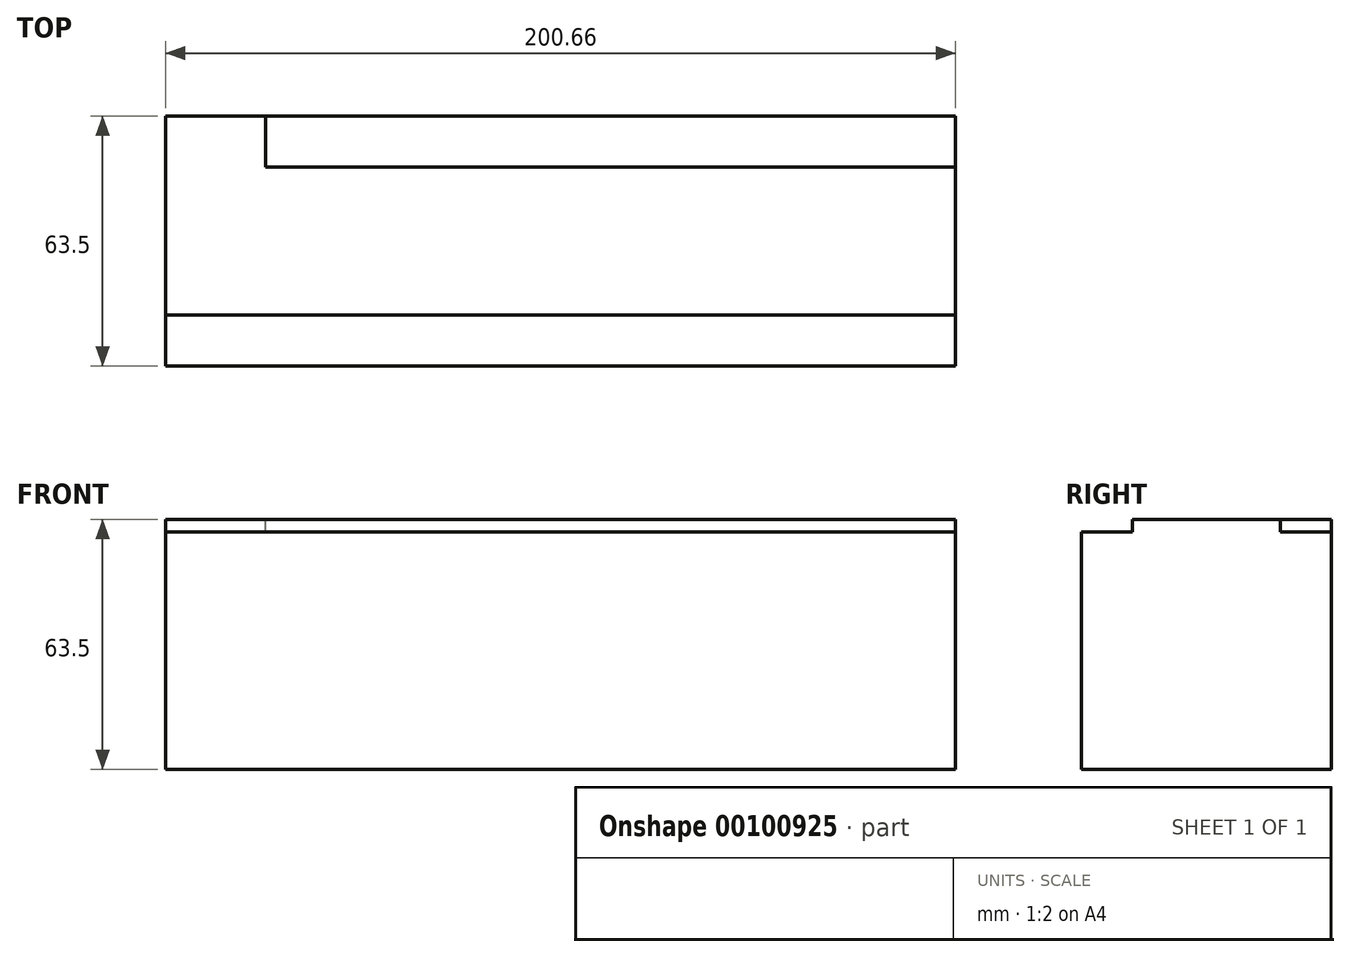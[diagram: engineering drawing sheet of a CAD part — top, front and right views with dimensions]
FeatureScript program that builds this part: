
annotation { "Feature Type Name" : "Feature", "Feature Type Description" : "" }
export const myFeature = defineFeature(function(context is Context, id is Id, definition is map)
    precondition{}
    {
        {
            var Q0;
            Q0=qCreatedBy(makeId("Top.planeOp"),FACE);
            var sketch = newSketch(context, id + "F0", { "sketchPlane" : qUnion([Q0])});
            skLineSegment(sketch, "E0.bottom", {"start": v(0, 0) * mm, "end": v(-200.66, 0) * mm});
            skLineSegment(sketch, "E0.top", {"start": v(0, 63.5) * mm, "end": v(-200.66, 63.5) * mm});
            skLineSegment(sketch, "E0.left", {"start": v(0, 0) * mm, "end": v(0, 63.5) * mm});
            skLineSegment(sketch, "E0.right", {"start": v(-200.66, 0) * mm, "end": v(-200.66, 63.5) * mm});
            skSolve(sketch);
        }
        {
            var Q0;
            Q0 = qSketchRegion(id + "F0", true);
            extrude(context, id + "F1", {"entities" : qUnion([Q0]), "oppositeDirection" : true, "depth" : 63.5 * mm});
        }
        {
            var Q0;
            Q0=makeQuery(id+"F1.opExtrude","CAP_FACE",FACE,{"disambiguationData":[OSD([sQuery(id+"F0.wireOp",EDGE,"E0.bottom"),sQuery(id+"F0.wireOp",EDGE,"E0.top"),sQuery(id+"F0.wireOp",EDGE,"E0.left"),sQuery(id+"F0.wireOp",EDGE,"E0.right")])],"isStart":true});
            var sketch = newSketch(context, id + "F2", { "sketchPlane" : qUnion([Q0])});
            skLineSegment(sketch, "E1.bottom", {"start": v(0, 0) * mm, "end": v(-200.66, 0) * mm});
            skLineSegment(sketch, "E1.top", {"start": v(0, 12.95) * mm, "end": v(-200.66, 12.95) * mm});
            skLineSegment(sketch, "E1.left", {"start": v(0, 0) * mm, "end": v(0, 12.95) * mm});
            skLineSegment(sketch, "E1.right", {"start": v(-200.66, 0) * mm, "end": v(-200.66, 12.95) * mm});
            skLineSegment(sketch, "E2.bottom", {"start": v(0, 63.5) * mm, "end": v(-175.26, 63.5) * mm});
            skLineSegment(sketch, "E2.top", {"start": v(0, 50.55) * mm, "end": v(-175.26, 50.55) * mm});
            skLineSegment(sketch, "E2.left", {"start": v(0, 63.5) * mm, "end": v(0, 50.55) * mm});
            skLineSegment(sketch, "E2.right", {"start": v(-175.26, 63.5) * mm, "end": v(-175.26, 50.55) * mm});
            skSolve(sketch);
        }
        {
            var Q0;
            Q0 = qSketchRegion(id + "F2", true);
            extrude(context, id + "F3", {"entities" : qUnion([Q0]), "operationType" : NewBodyOperationType.REMOVE, "oppositeDirection" : true, "depth" : 3.12 * mm});
        }
    });
